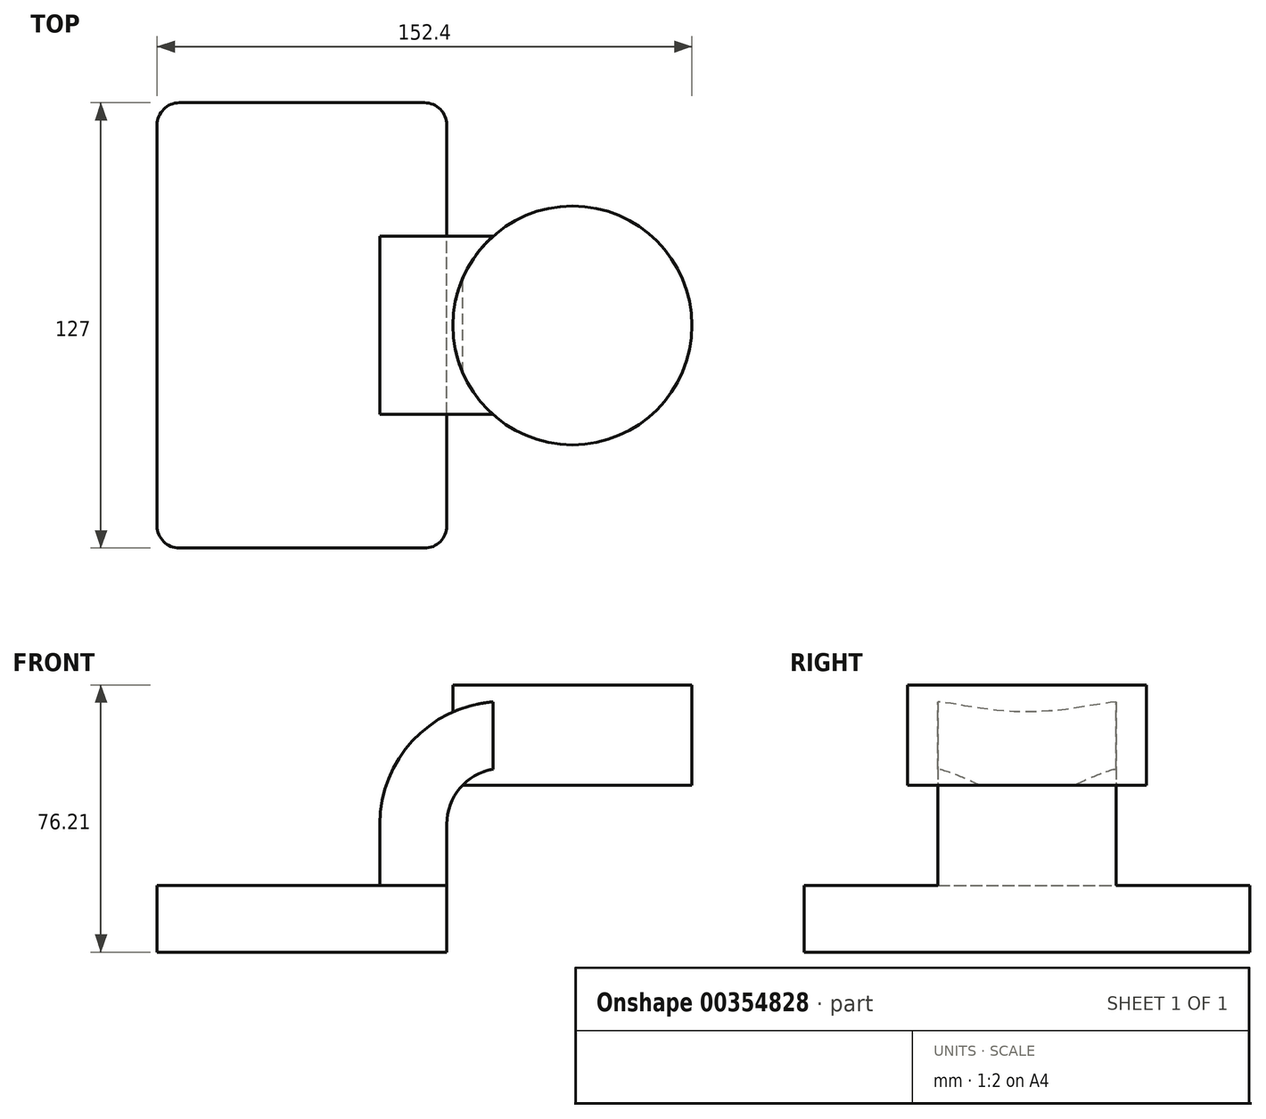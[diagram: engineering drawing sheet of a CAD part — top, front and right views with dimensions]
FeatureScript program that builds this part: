
annotation { "Feature Type Name" : "Feature", "Feature Type Description" : "" }
export const myFeature = defineFeature(function(context is Context, id is Id, definition is map)
    precondition{}
    {
        {
            var Q0;
            Q0=qCreatedBy(makeId("Front.planeOp"),FACE);
            var sketch = newSketch(context, id + "F0", { "sketchPlane" : qUnion([Q0])});
            skLineSegment(sketch, "E0.bottom", {"start": v(41.28, -9.52) * mm, "end": v(-41.28, -9.53) * mm});
            skLineSegment(sketch, "E0.top", {"start": v(41.28, 9.53) * mm, "end": v(-41.28, 9.53) * mm});
            skLineSegment(sketch, "E0.left", {"start": v(41.28, -9.52) * mm, "end": v(41.28, 9.53) * mm});
            skLineSegment(sketch, "E0.right", {"start": v(-41.28, -9.53) * mm, "end": v(-41.28, 9.53) * mm});
            skPoint(sketch, "E0.middle", {"position": v(0, 0) * mm});
            skLineSegment(sketch, "E1.bottom", {"start": v(111.12, 38.1) * mm, "end": v(60.32, 38.1) * mm});
            skLineSegment(sketch, "E1.top", {"start": v(111.12, 66.68) * mm, "end": v(60.32, 66.68) * mm});
            skLineSegment(sketch, "E1.left", {"start": v(111.12, 38.1) * mm, "end": v(111.12, 66.68) * mm});
            skLineSegment(sketch, "E1.right", {"start": v(60.32, 38.1) * mm, "end": v(60.32, 66.67) * mm});
            skPoint(sketch, "E1.middle", {"position": v(85.72, 52.39) * mm});
            skLineSegment(sketch, "E2", {"start": v(41.28, 9.53) * mm, "end": v(41.28, 27) * mm});
            skArc(sketch, "E3", {"start": v(41.27, 27) * mm, "mid": v(45.92, 38.23) * mm, "end": v(57.15, 42.88) * mm});
            skLineSegment(sketch, "E4", {"start": v(57.15, 42.88) * mm, "end": v(77.08, 42.88) * mm});
            skLineSegment(sketch, "E5.0", {"start": v(57.15, 61.93) * mm, "end": v(77.08, 61.93) * mm});
            skArc(sketch, "E5.1", {"start": v(22.23, 27) * mm, "mid": v(32.45, 51.7) * mm, "end": v(57.15, 61.93) * mm});
            skLineSegment(sketch, "E5.2", {"start": v(22.22, 9.53) * mm, "end": v(22.22, 27) * mm});
            skLineSegment(sketch, "E6", {"start": v(77.08, 66.68) * mm, "end": v(77.08, 38.1) * mm});
            skFitSpline(sketch, "E7", {"points": [v(-41.28, 9.53) * mm, v(57.15, 61.93) * mm], "startDerivative": vector(-0.33, 101.1) * mm, "endDerivative": vector(171.45, -6.32) * mm});
            skSolve(sketch);
        }
        {
            var Q0;
            Q0=qCreatedBy(makeId("Front.planeOp"),FACE);
            var sketch = newSketch(context, id + "F1", { "sketchPlane" : qUnion([Q0])});
            skSolve(sketch);
        }
        {
            var Q0;
            Q0=makeQuery(id+"F0.imprint","IMPRINT",FACE,{"disambiguationData":[TD([[makeQuery(id+"F0.imprint","IMPRINT",EDGE,{"derivedFrom":sQuery(id+"F0.wireOp",EDGE,"E0.bottom")}),-1.0]])]});
            extrude(context, id + "F2", {"entities" : qUnion([Q0]), "endBound" : BoundingType.SYMMETRIC, "depth" : 127 * mm});
        }
        {
            var Q0;
            Q0 = qSketchRegion(id + "F1", true);
            var Q1;
            {var subQ1=sQuery(id+"F0.wireOp",EDGE,"E2");Q1=makeQuery(id+"F0.imprint","IMPRINT",FACE,{"disambiguationData":[TD([[makeQuery(id+"F0.imprint","IMPRINT",EDGE,{"derivedFrom":subQ1}),1.0]])]});}
            var Q2;
            {var subQ0=sQuery(id+"F0.wireOp",EDGE,"E4");var subQ1=sQuery(id+"F0.wireOp",EDGE,"E1.right");var subQ2=makeQuery(id+"F0.imprint","INTERSECT",VERTEX,{"derivedFrom":[subQ1,subQ0]});Q2=makeQuery(id+"F0.imprint","IMPRINT",FACE,{"disambiguationData":[TD([[makeQuery(id+"F0.imprint","IMPRINT",EDGE,{"disambiguationData":[TD([[subQ2,-1.0]])],"derivedFrom":subQ1}),-1.0]])]});}
            extrude(context, id + "F3", {"entities" : qUnion([Q0, Q1, Q2]), "operationType" : NewBodyOperationType.ADD, "endBound" : BoundingType.SYMMETRIC, "depth" : 50.8 * mm});
        }
        {
            var Q0;
            Q0=makeQuery(id+"F0.imprint","IMPRINT",FACE,{"disambiguationData":[TD([[makeQuery(id+"F0.imprint","IMPRINT",EDGE,{"derivedFrom":sQuery(id+"F0.wireOp",EDGE,"E5.1")}),1.0]])]});
            extrude(context, id + "F4", {"entities" : qUnion([Q0]), "operationType" : NewBodyOperationType.ADD, "endBound" : BoundingType.SYMMETRIC, "depth" : 15.88 * mm});
        }
        {
            var Q0;
            {var subQ4=sQuery(id+"F0.wireOp",EDGE,"E1.left");Q0=makeQuery(id+"F0.imprint","IMPRINT",FACE,{"disambiguationData":[TD([[makeQuery(id+"F0.imprint","IMPRINT",EDGE,{"derivedFrom":subQ4}),1.0]])]});}
            var Q1;
            Q1=sQuery(id+"F0.wireOp",EDGE,"E6");
            revolve(context, id + "F5", {"operationType" : NewBodyOperationType.ADD, "entities" : qUnion([Q0]), "axis" : qUnion([Q1]), "revolveType" : RevolveType.FULL});
        }
        {
            var Q0;
            Q0=makeQuery(id+"F2.opExtrude","CAP_EDGE",EDGE,{"disambiguationData":[OSD([sQuery(id+"F0.wireOp",EDGE,"E0.left")])],"isStart":true});
            var Q1;
            Q1=makeQuery(id+"F2.opExtrude","CAP_EDGE",EDGE,{"disambiguationData":[OSD([sQuery(id+"F0.wireOp",EDGE,"E0.right")])],"isStart":true});
            var Q2;
            Q2=makeQuery(id+"F2.opExtrude","CAP_EDGE",EDGE,{"disambiguationData":[OSD([sQuery(id+"F0.wireOp",EDGE,"E0.left")])],"isStart":false});
            var Q3;
            Q3=makeQuery(id+"F2.opExtrude","CAP_EDGE",EDGE,{"disambiguationData":[OSD([sQuery(id+"F0.wireOp",EDGE,"E0.right")])],"isStart":false});
            var Q4;
            Q4=makeQuery(id+"F4.opExtrude","CAP_EDGE",EDGE,{"disambiguationData":[OSD([sQuery(id+"F0.wireOp",EDGE,"E0.top")])],"isStart":false});
            var Q5;
            Q5=makeQuery(id+"F4.opExtrude","CAP_EDGE",EDGE,{"disambiguationData":[OSD([sQuery(id+"F0.wireOp",EDGE,"E0.top")])],"isStart":true});
            var Q6;
            Q6=makeQuery(id+"F4.opExtrude","CAP_EDGE",EDGE,{"disambiguationData":[OSD([sQuery(id+"F0.wireOp",EDGE,"E5.2")])],"isStart":false});
            var Q7;
            Q7=makeQuery(id+"F4.opExtrude","CAP_EDGE",EDGE,{"disambiguationData":[OSD([sQuery(id+"F0.wireOp",EDGE,"E5.1")])],"isStart":true});
            fillet(context, id + "F6", {"entities" : qUnion([Q0, Q1, Q2, Q3, Q4, Q5, Q6, Q7]), "radius" : 6.35 * mm, "tangentPropagation" : true, "allowEdgeOverflow" : false});
        }
    });
